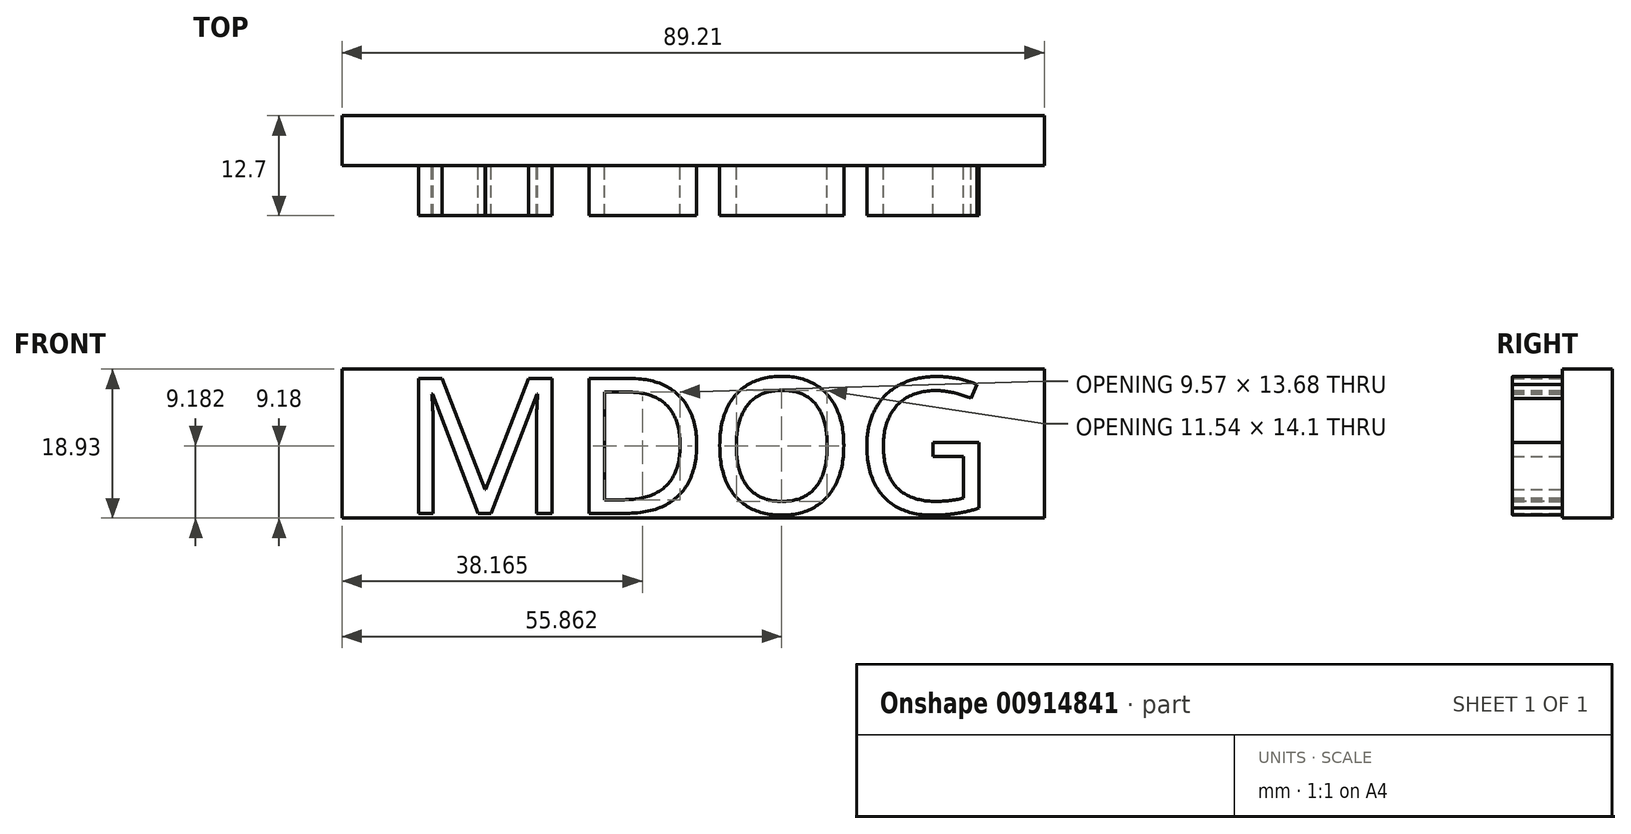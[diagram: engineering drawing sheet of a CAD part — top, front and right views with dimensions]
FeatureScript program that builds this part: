
annotation { "Feature Type Name" : "Feature", "Feature Type Description" : "" }
export const myFeature = defineFeature(function(context is Context, id is Id, definition is map)
    precondition{}
    {
        {
            var Q0;
            Q0=qCreatedBy(makeId("Front.planeOp"),FACE);
            var sketch = newSketch(context, id + "F0", { "sketchPlane" : qUnion([Q0])});
            skText(sketch, "E0", { "text": "MDOG", "fontName": "OpenSans-Regular.ttf"});
            const initialGuessF0  = {"E0": [-0.0387, 0.00993, 1, 0, 0.01727]};
            skSetInitialGuess(sketch, initialGuessF0);
            skSolve(sketch);
        }
        {
            var Q0;
            Q0 = qSketchRegion(id + "F0", true);
            extrude(context, id + "F1", {"entities" : qUnion([Q0]), "depth" : 6.35 * mm, "offsetDistance" : 25.4 * mm});
        }
        {
            var Q0;
            Q0=qCreatedBy(makeId("Front.planeOp"),FACE);
            var sketch = newSketch(context, id + "F2", { "sketchPlane" : qUnion([Q0])});
            skLineSegment(sketch, "E1.bottom", {"start": v(-46.08, 28.24) * mm, "end": v(43.13, 28.24) * mm});
            skLineSegment(sketch, "E1.top", {"start": v(-46.08, 9.31) * mm, "end": v(43.13, 9.31) * mm});
            skLineSegment(sketch, "E1.left", {"start": v(-46.08, 28.24) * mm, "end": v(-46.08, 9.31) * mm});
            skLineSegment(sketch, "E1.right", {"start": v(43.13, 28.24) * mm, "end": v(43.13, 9.31) * mm});
            skSolve(sketch);
        }
        {
            var Q0;
            Q0=makeQuery(id+"F2.imprint","IMPRINT",FACE,{"disambiguationData":[TD([[makeQuery(id+"F2.imprint","IMPRINT",EDGE,{"derivedFrom":sQuery(id+"F2.wireOp",EDGE,"E1.bottom")}),-1.0]])]});
            extrude(context, id + "F3", {"entities" : qUnion([Q0]), "oppositeDirection" : true, "depth" : 6.35 * mm, "offsetDistance" : 25.4 * mm});
        }
    });
